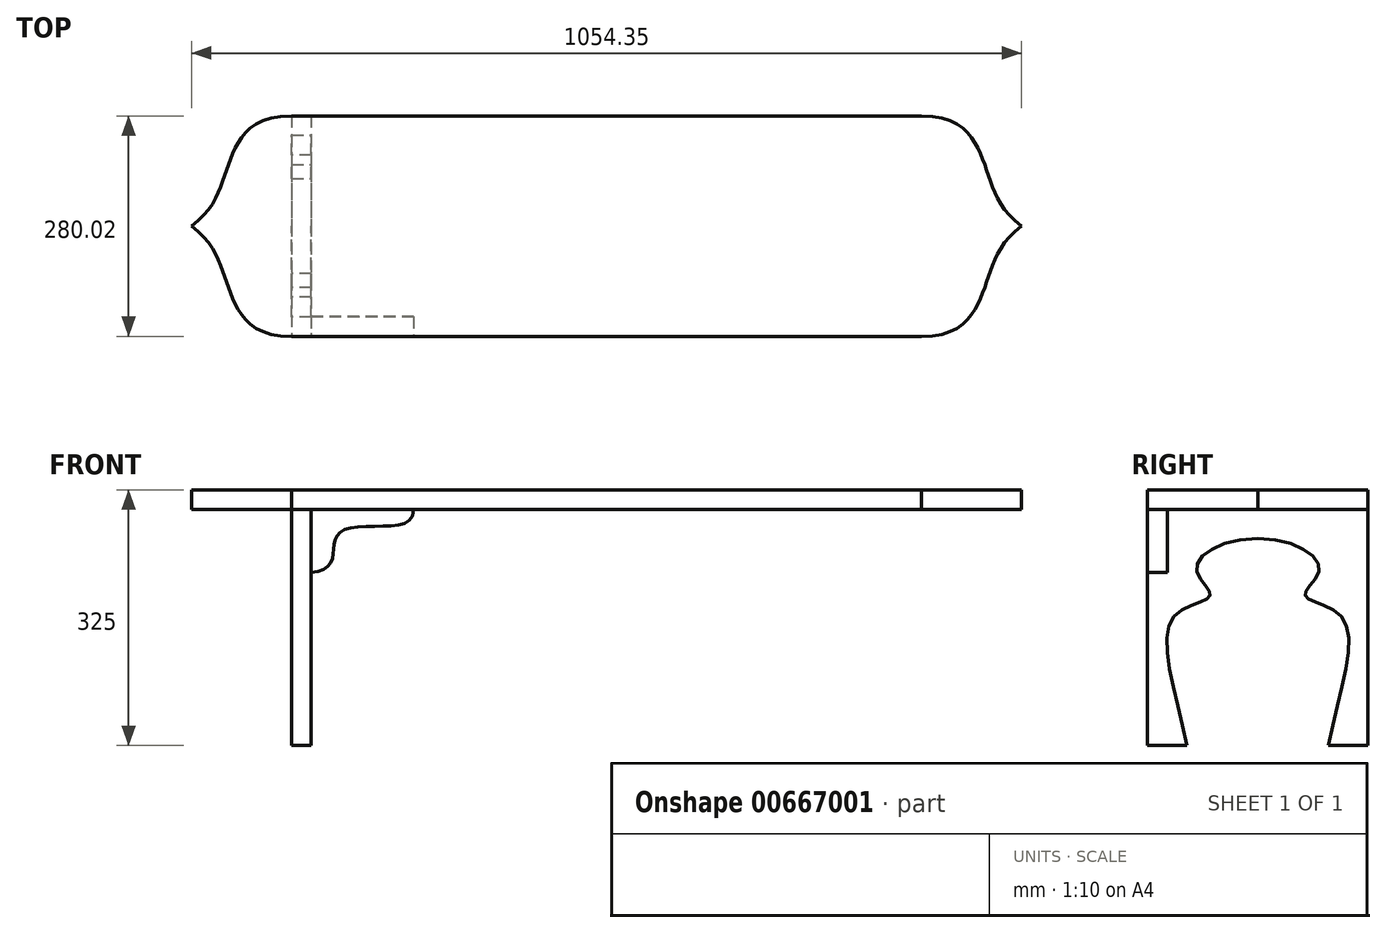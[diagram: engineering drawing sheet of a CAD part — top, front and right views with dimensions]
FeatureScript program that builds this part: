
annotation { "Feature Type Name" : "Feature", "Feature Type Description" : "" }
export const myFeature = defineFeature(function(context is Context, id is Id, definition is map)
    precondition{}
    {
        {
            var Q0;
            Q0=qCreatedBy(makeId("Top.planeOp"),FACE);
            var sketch = newSketch(context, id + "F0", { "sketchPlane" : qUnion([Q0])});
            skLineSegment(sketch, "E0.bottom", {"start": v(262.7, -49.5) * mm, "end": v(-537.3, -49.5) * mm});
            skLineSegment(sketch, "E0.top", {"start": v(262.7, 230.5) * mm, "end": v(-537.3, 230.5) * mm});
            skLineSegment(sketch, "E0.left", {"start": v(262.7, -49.5) * mm, "end": v(262.7, 230.5) * mm});
            skLineSegment(sketch, "E0.right", {"start": v(-537.3, -49.5) * mm, "end": v(-537.3, 230.5) * mm});
            skLineSegment(sketch, "E1", {"start": v(-137.3, 230.5) * mm, "end": v(-137.3, -323.2) * mm, "construction": true});
            skLineSegment(sketch, "E2", {"start": v(-817.62, 90.5) * mm, "end": v(-537.3, 90.5) * mm, "construction": true});
            skFitSpline(sketch, "E3", {"points": [v(-537.3, 230.5) * mm, v(-606.88, 193.32) * mm, v(-625.46, 146.25) * mm, v(-664.48, 90.5) * mm], "startDerivative": vector(-348.19, 5.02) * mm, "endDerivative": vector(-212.98, -158.37) * mm});
            skFitSpline(sketch, "E4.MirrorCS", {"points": [v(-537.3, -49.5) * mm, v(-606.88, -12.3) * mm, v(-625.46, 34.77) * mm, v(-664.48, 90.5) * mm], "startDerivative": vector(-348.19, -5.02) * mm, "endDerivative": vector(-212.98, 158.37) * mm});
            skFitSpline(sketch, "E5.MirrorCS", {"points": [v(262.7, 230.5) * mm, v(332.27, 193.32) * mm, v(350.85, 146.25) * mm, v(389.87, 90.5) * mm], "startDerivative": vector(348.19, 5.02) * mm, "endDerivative": vector(212.98, -158.37) * mm});
            skFitSpline(sketch, "E6.MirrorCS", {"points": [v(262.7, -49.5) * mm, v(332.27, -12.3) * mm, v(350.85, 34.77) * mm, v(389.87, 90.5) * mm], "startDerivative": vector(348.19, -5.02) * mm, "endDerivative": vector(212.98, 158.37) * mm});
            skSolve(sketch);
        }
        {
            var Q0;
            Q0=qCreatedBy(makeId("Right.planeOp"),FACE);
            var Q1;
            Q1=sQuery(id+"F0.wireOp",VERTEX,"E0.right.start");
            cPlane(context, id + "F1", {"entities" : qUnion([Q0, Q1]), "cplaneType" : CPlaneType.PLANE_POINT, "offset" : 25 * mm, "width" : 150 * mm, "height" : 150 * mm});
        }
        {
            var Q0;
            Q0=qCreatedBy(id+"F1.planeOp",FACE);
            var sketch = newSketch(context, id + "F2", { "sketchPlane" : qUnion([Q0])});
            skLineSegment(sketch, "E7.bottom", {"start": v(230.5, 0) * mm, "end": v(-49.5, 0) * mm});
            skLineSegment(sketch, "E7.top", {"start": v(230.5, -300) * mm, "end": v(-49.5, -300) * mm});
            skLineSegment(sketch, "E7.left", {"start": v(230.5, 0) * mm, "end": v(230.5, -300) * mm});
            skLineSegment(sketch, "E7.right", {"start": v(-49.5, 0) * mm, "end": v(-49.5, -300) * mm});
            skFitSpline(sketch, "E8", {"points": [v(180.5, -300) * mm, v(199.58, -139.86) * mm, v(155.1, -113.74) * mm, v(151.5, -104.66) * mm, v(168.42, -75.1) * mm, v(90.5, -36.63) * mm], "startDerivative": vector(112.2, 585.8) * mm, "endDerivative": vector(-539.6, 1.66) * mm});
            skLineSegment(sketch, "E9", {"start": v(90.5, 0) * mm, "end": v(90.5, -368.98) * mm, "construction": true});
            skFitSpline(sketch, "E10.MirrorCS", {"points": [v(0.5, -300) * mm, v(-18.56, -139.86) * mm, v(25.92, -113.74) * mm, v(29.52, -104.66) * mm, v(12.6, -75.1) * mm, v(90.5, -36.63) * mm], "startDerivative": vector(-112.2, 585.8) * mm, "endDerivative": vector(539.6, 1.66) * mm});
            skSolve(sketch);
        }
        {
            var Q0;
            Q0=makeQuery(id+"F0.imprint","IMPRINT",FACE,{"disambiguationData":[TD([[makeQuery(id+"F0.imprint","IMPRINT",EDGE,{"derivedFrom":sQuery(id+"F0.wireOp",EDGE,"E0.right")}),1.0]])]});
            var Q1;
            Q1=makeQuery(id+"F0.imprint","IMPRINT",FACE,{"disambiguationData":[TD([[makeQuery(id+"F0.imprint","IMPRINT",EDGE,{"derivedFrom":sQuery(id+"F0.wireOp",EDGE,"E0.bottom")}),-1.0]])]});
            var Q2;
            Q2=makeQuery(id+"F0.imprint","IMPRINT",FACE,{"disambiguationData":[TD([[makeQuery(id+"F0.imprint","IMPRINT",EDGE,{"derivedFrom":sQuery(id+"F0.wireOp",EDGE,"E0.left")}),-1.0]])]});
            extrude(context, id + "F3", {"entities" : qUnion([Q0, Q1, Q2]), "depth" : 25 * mm, "offsetDistance" : 25 * mm});
        }
        {
            var Q0;
            Q0=makeQuery(id+"F2.imprint","IMPRINT",FACE,{"disambiguationData":[TD([[makeQuery(id+"F2.imprint","IMPRINT",EDGE,{"derivedFrom":sQuery(id+"F2.wireOp",EDGE,"E7.bottom")}),1.0]])]});
            extrude(context, id + "F4", {"entities" : qUnion([Q0]), "depth" : 25 * mm, "offsetDistance" : 25 * mm});
        }
        {
            var Q0;
            Q0=makeQuery(id+"F4.opExtrude","SWEPT_FACE",FACE,{"disambiguationData":[OSD([sQuery(id+"F2.wireOp",EDGE,"E7.right")])]});
            var sketch = newSketch(context, id + "F5", { "sketchPlane" : qUnion([Q0])});
            skLineSegment(sketch, "E11", {"start": v(-382.3, 0) * mm, "end": v(-512.3, 0) * mm});
            skLineSegment(sketch, "E12", {"start": v(-512.3, 0) * mm, "end": v(-512.3, -80) * mm});
            skFitSpline(sketch, "E13", {"points": [v(-512.3, -80) * mm, v(-486.72, -65.78) * mm, v(-483.24, -42.86) * mm, v(-470.12, -25.65) * mm, v(-406.2, -20.27) * mm, v(-382.3, 0) * mm], "startDerivative": vector(221.47, 5.99) * mm, "endDerivative": vector(10.35, 226.8) * mm});
            skSolve(sketch);
        }
        {
            var Q0;
            Q0=makeQuery(id+"F5.imprint","IMPRINT",FACE,{"disambiguationData":[TD([[makeQuery(id+"F5.imprint","IMPRINT",EDGE,{"derivedFrom":sQuery(id+"F5.wireOp",EDGE,"E11")}),1.0]])]});
            extrude(context, id + "F6", {"entities" : qUnion([Q0]), "oppositeDirection" : true, "depth" : 25 * mm, "offsetDistance" : 25 * mm});
        }
    });
